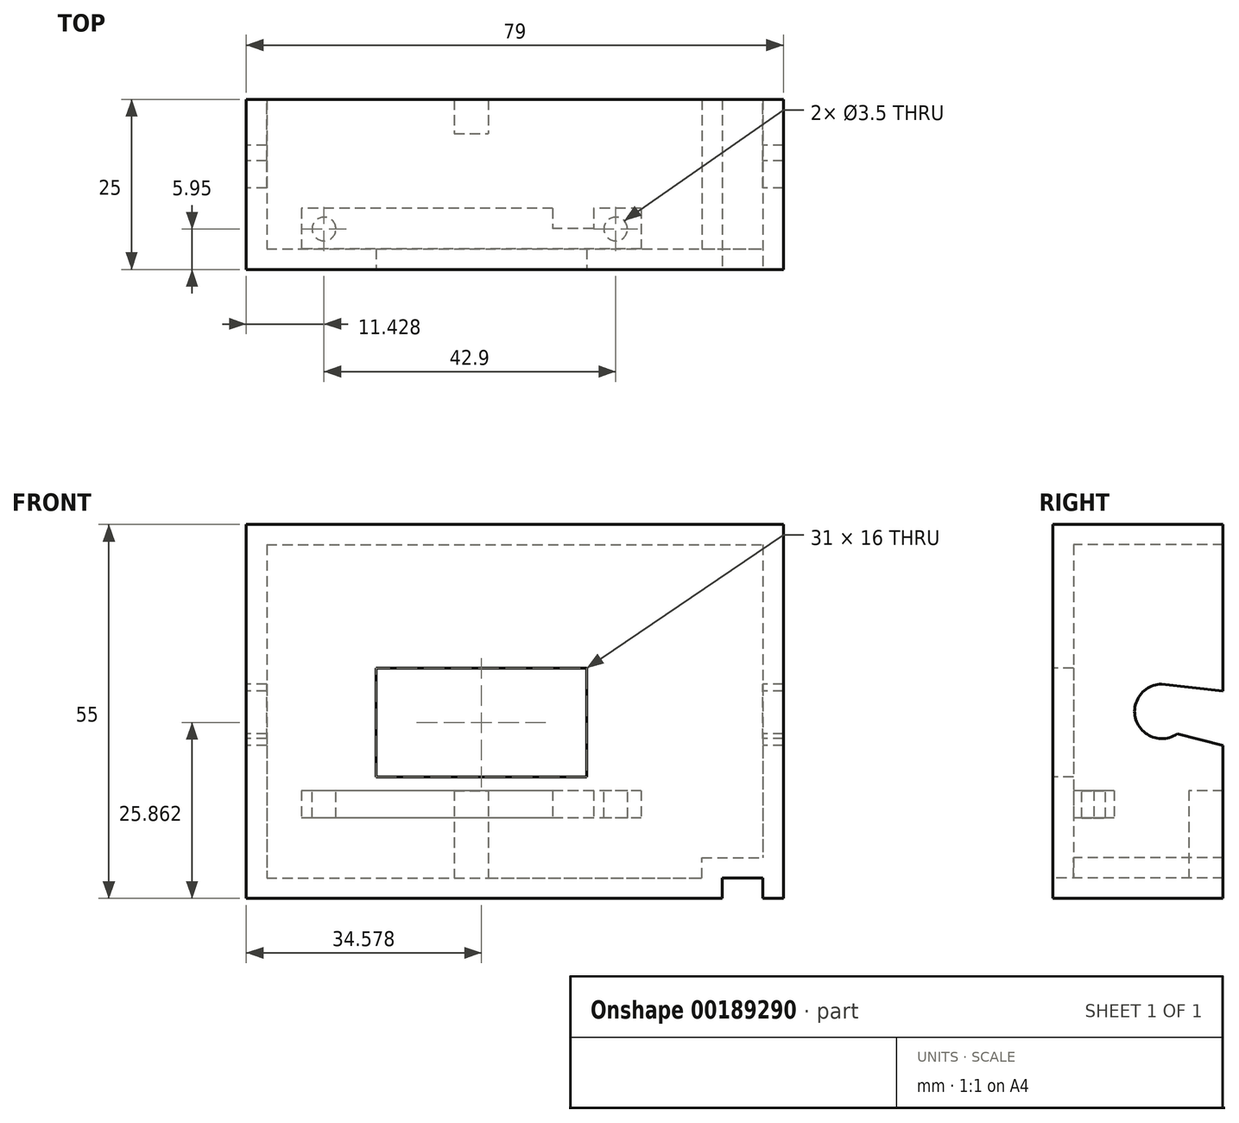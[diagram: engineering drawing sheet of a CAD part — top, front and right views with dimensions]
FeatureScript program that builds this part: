
annotation { "Feature Type Name" : "Feature", "Feature Type Description" : "" }
export const myFeature = defineFeature(function(context is Context, id is Id, definition is map)
    precondition{}
    {
        {
            var Q0;
            Q0=qCreatedBy(makeId("Front.planeOp"),FACE);
            var sketch = newSketch(context, id + "F0", { "sketchPlane" : qUnion([Q0])});
            skLineSegment(sketch, "E0.bottom", {"start": v(39.5, 27.5) * mm, "end": v(-39.5, 27.5) * mm});
            skLineSegment(sketch, "E0.top", {"start": v(39.5, -27.5) * mm, "end": v(-39.5, -27.5) * mm});
            skLineSegment(sketch, "E0.left", {"start": v(39.5, 27.5) * mm, "end": v(39.5, -27.5) * mm});
            skLineSegment(sketch, "E0.right", {"start": v(-39.5, 27.5) * mm, "end": v(-39.5, -27.5) * mm});
            skPoint(sketch, "E0.middle", {"position": v(0, 0) * mm});
            skLineSegment(sketch, "E1.bottom", {"start": v(-36.5, 24.5) * mm, "end": v(36.5, 24.5) * mm});
            skLineSegment(sketch, "E1.top", {"start": v(-36.5, -24.5) * mm, "end": v(36.5, -24.5) * mm});
            skLineSegment(sketch, "E1.left", {"start": v(-36.5, 24.5) * mm, "end": v(-36.5, -24.5) * mm});
            skLineSegment(sketch, "E1.right", {"start": v(36.5, 24.5) * mm, "end": v(36.5, -24.5) * mm});
            skLineSegment(sketch, "E2.bottom", {"start": v(-20.42, 6.36) * mm, "end": v(10.58, 6.36) * mm});
            skLineSegment(sketch, "E2.top", {"start": v(-20.42, -9.64) * mm, "end": v(10.58, -9.64) * mm});
            skLineSegment(sketch, "E2.left", {"start": v(-20.42, 6.36) * mm, "end": v(-20.42, -9.64) * mm});
            skLineSegment(sketch, "E2.right", {"start": v(10.58, 6.36) * mm, "end": v(10.58, -9.64) * mm});
            skLineSegment(sketch, "E3", {"start": v(-35.42, -9.64) * mm, "end": v(17.58, -9.64) * mm, "construction": true});
            skPoint(sketch, "E4", {"position": v(-6.42, -9.64) * mm});
            skSolve(sketch);
        }
        {
            var Q0;
            Q0=makeQuery(id+"F0.imprint","IMPRINT",FACE,{"disambiguationData":[TD([[makeQuery(id+"F0.imprint","IMPRINT",EDGE,{"derivedFrom":sQuery(id+"F0.wireOp",EDGE,"E0.bottom")}),1.0]])]});
            extrude(context, id + "F1", {"entities" : qUnion([Q0]), "oppositeDirection" : true, "depth" : 25 * mm});
        }
        {
            var Q0;
            Q0=makeQuery(id+"F1.opExtrude","SWEPT_FACE",FACE,{"disambiguationData":[OSD([sQuery(id+"F0.wireOp",EDGE,"E0.right")])]});
            var sketch = newSketch(context, id + "F2", { "sketchPlane" : qUnion([Q0])});
            skArc(sketch, "E5", {"start": v(-18.27, -3.3) * mm, "mid": v(-12.07, -0.76) * mm, "end": v(-16.88, 3.9) * mm});
            skPoint(sketch, "E6", {"position": v(-16, 4) * mm});
            skPoint(sketch, "E7", {"position": v(-18.27, -3.3) * mm});
            skLineSegment(sketch, "E8", {"start": v(-16, 4) * mm, "end": v(-25, 3) * mm});
            skLineSegment(sketch, "E9", {"start": v(-18.27, -3.3) * mm, "end": v(-25, -5) * mm});
            skSolve(sketch);
        }
        {
            var Q0;
            {var subQ0=sQuery(id+"F2.wireOp",EDGE,"E9");Q0=makeQuery(id+"F2.imprint","IMPRINT",FACE,{"disambiguationData":[TD([[makeQuery(id+"F2.imprint","IMPRINT",EDGE,{"derivedFrom":subQ0}),-1.0]])]});}
            var Q1;
            Q1=makeQuery(id+"F1.opExtrude","SWEPT_FACE",FACE,{"disambiguationData":[OSD([sQuery(id+"F0.wireOp",EDGE,"E0.left")])]});
            extrude(context, id + "F3", {"entities" : qUnion([Q0]), "operationType" : NewBodyOperationType.REMOVE, "endBound" : BoundingType.UP_TO_SURFACE, "oppositeDirection" : true, "endBoundEntityFace" : qUnion([Q1]), "depth" : 23 * mm});
        }
        {
            var Q0;
            Q0=makeQuery(id+"F0.imprint","IMPRINT",FACE,{"disambiguationData":[TD([[makeQuery(id+"F0.imprint","IMPRINT",EDGE,{"derivedFrom":sQuery(id+"F0.wireOp",EDGE,"E1.bottom")}),-1.0]])]});
            extrude(context, id + "F4", {"entities" : qUnion([Q0]), "operationType" : NewBodyOperationType.ADD, "oppositeDirection" : true, "depth" : 3 * mm});
        }
        {
            var Q0;
            Q0=makeQuery(id+"F4.opExtrude","CAP_FACE",FACE,{"disambiguationData":[OSD([sQuery(id+"F0.wireOp",EDGE,"E1.bottom"),sQuery(id+"F0.wireOp",EDGE,"E1.top"),sQuery(id+"F0.wireOp",EDGE,"E1.left"),sQuery(id+"F0.wireOp",EDGE,"E1.right"),sQuery(id+"F0.wireOp",EDGE,"E2.bottom"),sQuery(id+"F0.wireOp",EDGE,"E2.top"),sQuery(id+"F0.wireOp",EDGE,"E2.left"),sQuery(id+"F0.wireOp",EDGE,"E2.right")])],"isStart":false});
            var sketch = newSketch(context, id + "F5", { "sketchPlane" : qUnion([Q0])});
            skLineSegment(sketch, "E10.bottom", {"start": v(-18.58, -11.64) * mm, "end": v(31.42, -11.64) * mm});
            skLineSegment(sketch, "E10.top", {"start": v(-18.58, -15.64) * mm, "end": v(31.42, -15.64) * mm});
            skLineSegment(sketch, "E10.left", {"start": v(-18.58, -11.64) * mm, "end": v(-18.58, -15.64) * mm});
            skLineSegment(sketch, "E10.right", {"start": v(31.42, -11.64) * mm, "end": v(31.42, -15.64) * mm});
            skLineSegment(sketch, "E11", {"start": v(-11.58, -11.64) * mm, "end": v(-11.58, -15.64) * mm});
            skLineSegment(sketch, "E12", {"start": v(-5.58, -11.64) * mm, "end": v(-5.58, -15.64) * mm});
            skSolve(sketch);
        }
        {
            var Q0;
            {var subQ0=sQuery(id+"F5.wireOp",EDGE,"E11");Q0=makeQuery(id+"F5.imprint","IMPRINT",FACE,{"disambiguationData":[TD([[makeQuery(id+"F5.imprint","IMPRINT",EDGE,{"derivedFrom":subQ0}),1.0]])]});}
            extrude(context, id + "F6", {"entities" : qUnion([Q0]), "operationType" : NewBodyOperationType.ADD, "depth" : 3 * mm});
        }
        {
            var Q0;
            {var subQ0=sQuery(id+"F5.wireOp",EDGE,"E10.right");Q0=makeQuery(id+"F5.imprint","IMPRINT",FACE,{"disambiguationData":[TD([[makeQuery(id+"F5.imprint","IMPRINT",EDGE,{"derivedFrom":subQ0}),-1.0]])]});}
            var Q1;
            {var subQ0=sQuery(id+"F5.wireOp",EDGE,"E10.left");Q1=makeQuery(id+"F5.imprint","IMPRINT",FACE,{"disambiguationData":[TD([[makeQuery(id+"F5.imprint","IMPRINT",EDGE,{"derivedFrom":subQ0}),1.0]])]});}
            extrude(context, id + "F7", {"entities" : qUnion([Q0, Q1]), "operationType" : NewBodyOperationType.ADD, "depth" : 6 * mm});
        }
        {
            var Q0;
            Q0=makeQuery(id+"F1.opExtrude","SWEPT_FACE",FACE,{"disambiguationData":[OSD([sQuery(id+"F0.wireOp",EDGE,"E1.top")])]});
            var sketch = newSketch(context, id + "F8", { "sketchPlane" : qUnion([Q0])});
            skLineSegment(sketch, "E13.bottom", {"start": v(-8.92, 25) * mm, "end": v(-3.92, 25) * mm});
            skLineSegment(sketch, "E13.top", {"start": v(-8.92, 20) * mm, "end": v(-3.92, 20) * mm});
            skLineSegment(sketch, "E13.left", {"start": v(-8.92, 25) * mm, "end": v(-8.92, 20) * mm});
            skLineSegment(sketch, "E13.right", {"start": v(-3.92, 25) * mm, "end": v(-3.92, 20) * mm});
            skPoint(sketch, "E14", {"position": v(-6.42, 20) * mm});
            skSolve(sketch);
        }
        {
            var Q0;
            Q0=makeQuery(id+"F8.imprint","IMPRINT",FACE,{"disambiguationData":[TD([[makeQuery(id+"F8.imprint","IMPRINT",EDGE,{"derivedFrom":sQuery(id+"F8.wireOp",EDGE,"E13.bottom")}),-1.0]])]});
            extrude(context, id + "F9", {"entities" : qUnion([Q0]), "operationType" : NewBodyOperationType.ADD, "depth" : 12.86 * mm});
        }
        {
            var Q0;
            {var subQ0=sQuery(id+"F5.wireOp",EDGE,"E10.bottom");Q0=makeQuery(id+"F7.boolean.opBoolean","MERGE",FACE,{"derivedFrom":[makeQuery(id+"F6.opExtrude","SWEPT_FACE",FACE,{"disambiguationData":[OSD([subQ0])]}),makeQuery(id+"F7.opExtrude","SWEPT_FACE",FACE,{"disambiguationData":[OSD([subQ0]),TDD([makeQuery(id+"F5.imprint","IMPRINT",EDGE,{"disambiguationData":[TD([[makeQuery(id+"F5.imprint","INTERSECT",VERTEX,{"derivedFrom":[subQ0,sQuery(id+"F5.wireOp",EDGE,"E10.left")]}),-1.0]])],"derivedFrom":subQ0})])]}),makeQuery(id+"F7.opExtrude","SWEPT_FACE",FACE,{"disambiguationData":[OSD([subQ0]),TDD([makeQuery(id+"F5.imprint","IMPRINT",EDGE,{"disambiguationData":[TD([[makeQuery(id+"F5.imprint","INTERSECT",VERTEX,{"derivedFrom":[subQ0,sQuery(id+"F5.wireOp",EDGE,"E10.right")]}),1.0]])],"derivedFrom":subQ0})])]})]});}
            var sketch = newSketch(context, id + "F10", { "sketchPlane" : qUnion([Q0])});
            skCircle(sketch, "E15", {"center": v(14.83, 5.95) * mm, "radius": 1.75 * mm});
            skPoint(sketch, "E16", {"position": v(14.83, 4.2) * mm});
            skPoint(sketch, "E17", {"position": v(16.58, 5.95) * mm});
            skCircle(sketch, "E18", {"center": v(-28.07, 5.95) * mm, "radius": 1.75 * mm});
            skPoint(sketch, "E19", {"position": v(-28.07, 4.2) * mm});
            skPoint(sketch, "E20", {"position": v(-29.82, 5.95) * mm});
            skPoint(sketch, "E21", {"position": v(13.08, 5.95) * mm});
            skPoint(sketch, "E22", {"position": v(-26.32, 5.95) * mm});
            skSolve(sketch);
        }
        {
            var Q0;
            Q0=makeQuery(id+"F10.imprint","IMPRINT",FACE,{"disambiguationData":[TD([[makeQuery(id+"F10.imprint","IMPRINT",EDGE,{"derivedFrom":sQuery(id+"F10.wireOp",EDGE,"E15")}),1.0]])]});
            var Q1;
            Q1=makeQuery(id+"F10.imprint","IMPRINT",FACE,{"disambiguationData":[TD([[makeQuery(id+"F10.imprint","IMPRINT",EDGE,{"derivedFrom":sQuery(id+"F10.wireOp",EDGE,"E18")}),1.0]])]});
            var Q2;
            {var subQ0=sQuery(id+"F5.wireOp",EDGE,"E10.top");Q2=makeQuery(id+"F7.boolean.opBoolean","MERGE",FACE,{"derivedFrom":[makeQuery(id+"F6.opExtrude","SWEPT_FACE",FACE,{"disambiguationData":[OSD([subQ0])]}),makeQuery(id+"F7.opExtrude","SWEPT_FACE",FACE,{"disambiguationData":[OSD([subQ0]),TDD([makeQuery(id+"F5.imprint","IMPRINT",EDGE,{"disambiguationData":[TD([[makeQuery(id+"F5.imprint","INTERSECT",VERTEX,{"derivedFrom":[subQ0,sQuery(id+"F5.wireOp",EDGE,"E10.left")]}),-1.0]])],"derivedFrom":subQ0})])]}),makeQuery(id+"F7.opExtrude","SWEPT_FACE",FACE,{"disambiguationData":[OSD([subQ0]),TDD([makeQuery(id+"F5.imprint","IMPRINT",EDGE,{"disambiguationData":[TD([[makeQuery(id+"F5.imprint","INTERSECT",VERTEX,{"derivedFrom":[subQ0,sQuery(id+"F5.wireOp",EDGE,"E10.right")]}),1.0]])],"derivedFrom":subQ0})])]})]});}
            extrude(context, id + "F11", {"entities" : qUnion([Q0, Q1]), "operationType" : NewBodyOperationType.REMOVE, "endBound" : BoundingType.UP_TO_SURFACE, "oppositeDirection" : true, "endBoundEntityFace" : qUnion([Q2]), "depth" : 25 * mm});
        }
        {
            var Q0;
            {var subQ0=sQuery(id+"F0.wireOp",EDGE,"E1.right");var subQ1=sQuery(id+"F0.wireOp",EDGE,"E1.left");var subQ2=sQuery(id+"F0.wireOp",EDGE,"E1.top");var subQ3=sQuery(id+"F0.wireOp",EDGE,"E1.bottom");Q0=makeQuery(id+"F4.boolean.opBoolean","MERGE",FACE,{"derivedFrom":[makeQuery(id+"F1.opExtrude","CAP_FACE",FACE,{"disambiguationData":[OSD([sQuery(id+"F0.wireOp",EDGE,"E0.bottom"),sQuery(id+"F0.wireOp",EDGE,"E0.top"),sQuery(id+"F0.wireOp",EDGE,"E0.left"),sQuery(id+"F0.wireOp",EDGE,"E0.right"),subQ3,subQ2,subQ1,subQ0])],"isStart":true}),makeQuery(id+"F4.opExtrude","CAP_FACE",FACE,{"disambiguationData":[OSD([subQ3,subQ2,subQ1,subQ0,sQuery(id+"F0.wireOp",EDGE,"E2.bottom"),sQuery(id+"F0.wireOp",EDGE,"E2.top"),sQuery(id+"F0.wireOp",EDGE,"E2.left"),sQuery(id+"F0.wireOp",EDGE,"E2.right")])],"isStart":true})]});}
            var sketch = newSketch(context, id + "F12", { "sketchPlane" : qUnion([Q0])});
            skLineSegment(sketch, "E23.bottom", {"start": v(36.5, -27.5) * mm, "end": v(30.5, -27.5) * mm});
            skLineSegment(sketch, "E23.top", {"start": v(36.5, -24.5) * mm, "end": v(30.5, -24.5) * mm});
            skLineSegment(sketch, "E23.left", {"start": v(36.5, -27.5) * mm, "end": v(36.5, -24.5) * mm});
            skLineSegment(sketch, "E23.right", {"start": v(30.5, -27.5) * mm, "end": v(30.5, -24.5) * mm});
            skLineSegment(sketch, "E24.bottom", {"start": v(27.5, -27.5) * mm, "end": v(36.5, -27.5) * mm});
            skLineSegment(sketch, "E24.top", {"start": v(27.5, -21.5) * mm, "end": v(36.5, -21.5) * mm});
            skLineSegment(sketch, "E24.left", {"start": v(27.5, -27.5) * mm, "end": v(27.5, -21.5) * mm});
            skLineSegment(sketch, "E24.right", {"start": v(36.5, -27.5) * mm, "end": v(36.5, -21.5) * mm});
            skSolve(sketch);
        }
        {
            var Q0;
            {var subQ0=sQuery(id+"F12.wireOp",EDGE,"E23.top");Q0=makeQuery(id+"F12.imprint","IMPRINT",FACE,{"disambiguationData":[TD([[makeQuery(id+"F12.imprint","IMPRINT",EDGE,{"derivedFrom":subQ0}),1.0]])]});}
            var Q1;
            {var subQ0=sQuery(id+"F0.wireOp",EDGE,"E1.top");var subQ1=sQuery(id+"F0.wireOp",EDGE,"E0.right");var subQ2=sQuery(id+"F0.wireOp",EDGE,"E0.left");var subQ3=sQuery(id+"F0.wireOp",EDGE,"E0.top");var subQ4=sQuery(id+"F0.wireOp",EDGE,"E1.left");var subQ5=sQuery(id+"F0.wireOp",EDGE,"E1.right");Q1=makeQuery(id+"F9.boolean.opBoolean","MERGE",FACE,{"derivedFrom":[makeQuery(id+"F3.boolean.opBoolean","SPLIT",FACE,{"disambiguationData":[TD([makeQuery(id+"F1.opExtrude","SWEPT_FACE",FACE,{"disambiguationData":[OSD([subQ3])]})])],"derivedFrom":makeQuery(id+"F1.opExtrude","CAP_FACE",FACE,{"disambiguationData":[OSD([sQuery(id+"F0.wireOp",EDGE,"E0.bottom"),subQ3,subQ2,subQ1,sQuery(id+"F0.wireOp",EDGE,"E1.bottom"),subQ0,subQ4,subQ5])],"isStart":false})}),makeQuery(id+"F9.opExtrude","SWEPT_FACE",FACE,{"disambiguationData":[OSD([sQuery(id+"F8.wireOp",EDGE,"E13.bottom")])]})]});}
            extrude(context, id + "F13", {"entities" : qUnion([Q0]), "operationType" : NewBodyOperationType.REMOVE, "endBound" : BoundingType.UP_TO_SURFACE, "oppositeDirection" : true, "depth" : 25 * mm, "endBoundEntityFace" : qUnion([Q1]), "offsetDistance" : 25 * mm});
        }
        {
            var Q0;
            {var subQ4=sQuery(id+"F12.wireOp",EDGE,"E23.top");Q0=makeQuery(id+"F12.imprint","IMPRINT",FACE,{"disambiguationData":[TD([[makeQuery(id+"F12.imprint","IMPRINT",EDGE,{"derivedFrom":subQ4}),-1.0]])]});}
            var Q1;
            {var subQ0=sQuery(id+"F0.wireOp",EDGE,"E1.right");var subQ1=sQuery(id+"F0.wireOp",EDGE,"E1.left");var subQ2=sQuery(id+"F0.wireOp",EDGE,"E1.top");var subQ3=sQuery(id+"F0.wireOp",EDGE,"E0.right");var subQ4=sQuery(id+"F0.wireOp",EDGE,"E0.left");var subQ5=sQuery(id+"F0.wireOp",EDGE,"E0.top");var subQ6=makeQuery(id+"F1.opExtrude","CAP_FACE",FACE,{"disambiguationData":[OSD([sQuery(id+"F0.wireOp",EDGE,"E0.bottom"),subQ5,subQ4,subQ3,sQuery(id+"F0.wireOp",EDGE,"E1.bottom"),subQ2,subQ1,subQ0])],"isStart":false});var subQ7=makeQuery(id+"F1.opExtrude","SWEPT_FACE",FACE,{"disambiguationData":[OSD([subQ4])]});var subQ10=makeQuery(id+"F1.opExtrude","SWEPT_FACE",FACE,{"disambiguationData":[OSD([subQ5])]});Q1=makeQuery(id+"F13.boolean.opBoolean","SPLIT",FACE,{"disambiguationData":[TD([subQ7])],"derivedFrom":makeQuery(id+"F9.boolean.opBoolean","MERGE",FACE,{"derivedFrom":[makeQuery(id+"F3.boolean.opBoolean","SPLIT",FACE,{"disambiguationData":[TD([subQ10])],"derivedFrom":subQ6}),makeQuery(id+"F9.opExtrude","SWEPT_FACE",FACE,{"disambiguationData":[OSD([sQuery(id+"F8.wireOp",EDGE,"E13.bottom")])]})]})});}
            extrude(context, id + "F14", {"entities" : qUnion([Q0]), "operationType" : NewBodyOperationType.ADD, "endBound" : BoundingType.UP_TO_SURFACE, "oppositeDirection" : true, "depth" : 25 * mm, "endBoundEntityFace" : qUnion([Q1]), "offsetDistance" : 25 * mm});
        }
    });
